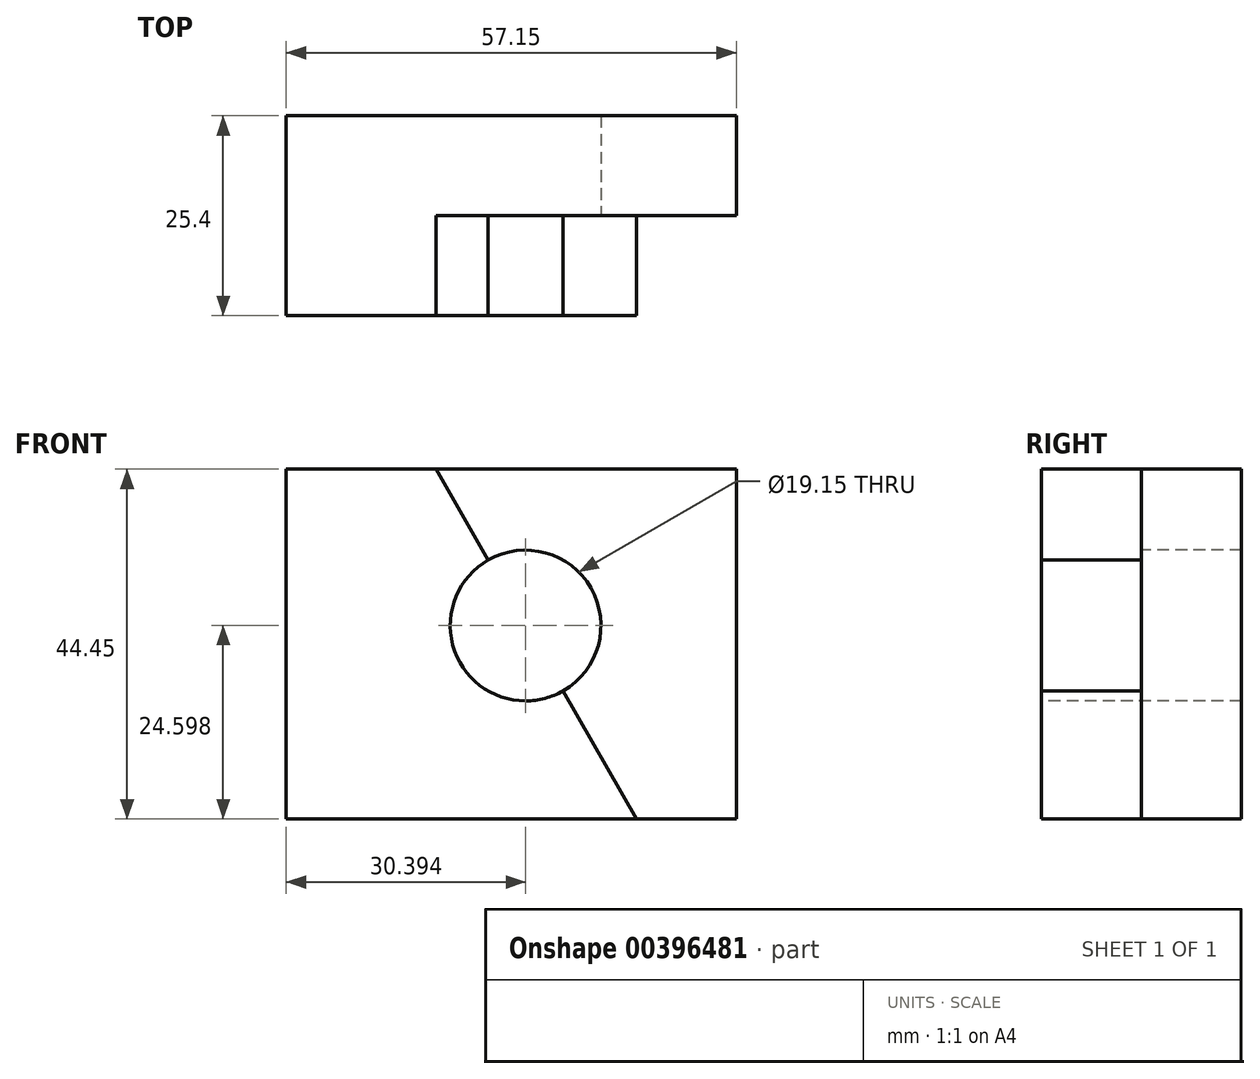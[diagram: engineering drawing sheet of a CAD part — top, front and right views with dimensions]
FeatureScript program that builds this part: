
annotation { "Feature Type Name" : "Feature", "Feature Type Description" : "" }
export const myFeature = defineFeature(function(context is Context, id is Id, definition is map)
    precondition{}
    {
        {
            var Q0;
            Q0=qCreatedBy(makeId("Front.planeOp"),FACE);
            var sketch = newSketch(context, id + "F0", { "sketchPlane" : qUnion([Q0])});
            skLineSegment(sketch, "E0", {"start": v(0, 0) * mm, "end": v(0, 44.45) * mm});
            skLineSegment(sketch, "E1", {"start": v(0, 44.45) * mm, "end": v(57.15, 44.45) * mm});
            skLineSegment(sketch, "E2", {"start": v(57.15, 44.45) * mm, "end": v(57.15, 0) * mm});
            skLineSegment(sketch, "E3", {"start": v(57.15, 0) * mm, "end": v(0, 0) * mm});
            skSolve(sketch);
        }
        {
            var Q0;
            Q0=makeQuery(id+"F0.imprint","IMPRINT",FACE,{"disambiguationData":[TD([[makeQuery(id+"F0.imprint","IMPRINT",EDGE,{"derivedFrom":sQuery(id+"F0.wireOp",EDGE,"E0")}),-1.0]])]});
            extrude(context, id + "F1", {"entities" : qUnion([Q0]), "depth" : 25.4 * mm});
        }
        {
            var Q0;
            Q0=makeQuery(id+"F1.opExtrude","CAP_FACE",FACE,{"disambiguationData":[OSD([sQuery(id+"F0.wireOp",EDGE,"E0"),sQuery(id+"F0.wireOp",EDGE,"E1"),sQuery(id+"F0.wireOp",EDGE,"E2"),sQuery(id+"F0.wireOp",EDGE,"E3")])],"isStart":false});
            var sketch = newSketch(context, id + "F2", { "sketchPlane" : qUnion([Q0])});
            skLineSegment(sketch, "E4", {"start": v(0, 0) * mm, "end": v(0, 44.45) * mm});
            skLineSegment(sketch, "E5", {"start": v(0, 44.45) * mm, "end": v(19.05, 44.45) * mm});
            skLineSegment(sketch, "E6", {"start": v(19.05, 44.45) * mm, "end": v(44.45, 0) * mm});
            skSolve(sketch);
        }
        {
            var Q0;
            {var subQ0=sQuery(id+"F2.wireOp",EDGE,"E6");Q0=makeQuery(id+"F2.imprint","IMPRINT",FACE,{"disambiguationData":[TD([[makeQuery(id+"F2.imprint","IMPRINT",EDGE,{"derivedFrom":subQ0}),1.0]])]});}
            extrude(context, id + "F3", {"entities" : qUnion([Q0]), "operationType" : NewBodyOperationType.REMOVE, "oppositeDirection" : true, "depth" : 12.7 * mm});
        }
        {
            var Q0;
            Q0=makeQuery(id+"F1.opExtrude","CAP_FACE",FACE,{"disambiguationData":[OSD([sQuery(id+"F0.wireOp",EDGE,"E0"),sQuery(id+"F0.wireOp",EDGE,"E1"),sQuery(id+"F0.wireOp",EDGE,"E2"),sQuery(id+"F0.wireOp",EDGE,"E3")])],"isStart":false});
            var sketch = newSketch(context, id + "F4", { "sketchPlane" : qUnion([Q0])});
            skCircle(sketch, "E7", {"center": v(30.4, 24.6) * mm, "radius": 9.57 * mm});
            skSolve(sketch);
        }
        {
            var Q0;
            {var subQ0=sQuery(id+"F4.wireOp",EDGE,"E7");var subQ1=makeQuery(id+"F3.boolean.opBoolean","COPY",EDGE,{"derivedFrom":makeQuery(id+"F3.opExtrude","CAP_EDGE",EDGE,{"disambiguationData":[OSD([sQuery(id+"F2.wireOp",EDGE,"E6")])],"isStart":true})});var subQ2=makeQuery(id+"F4.imprint","INTERSECT",VERTEX,{"disambiguationData":[OD(0.0)],"derivedFrom":[subQ1,subQ0]});Q0=makeQuery(id+"F4.imprint","IMPRINT",FACE,{"disambiguationData":[TD([[makeQuery(id+"F4.imprint","IMPRINT",EDGE,{"disambiguationData":[TD([[subQ2,1.0]])],"derivedFrom":subQ0}),1.0]])]});}
            var Q1;
            {var subQ0=sQuery(id+"F4.wireOp",EDGE,"E7");var subQ1=makeQuery(id+"F3.boolean.opBoolean","COPY",EDGE,{"derivedFrom":makeQuery(id+"F3.opExtrude","CAP_EDGE",EDGE,{"disambiguationData":[OSD([sQuery(id+"F2.wireOp",EDGE,"E6")])],"isStart":true})});var subQ2=makeQuery(id+"F4.imprint","INTERSECT",VERTEX,{"disambiguationData":[OD(0.0)],"derivedFrom":[subQ1,subQ0]});Q1=makeQuery(id+"F4.imprint","IMPRINT",FACE,{"disambiguationData":[TD([[makeQuery(id+"F4.imprint","IMPRINT",EDGE,{"disambiguationData":[TD([[subQ2,-1.0]])],"derivedFrom":subQ0}),1.0]])]});}
            extrude(context, id + "F5", {"entities" : qUnion([Q0, Q1]), "operationType" : NewBodyOperationType.REMOVE, "oppositeDirection" : true, "depth" : 25.4 * mm});
        }
    });
